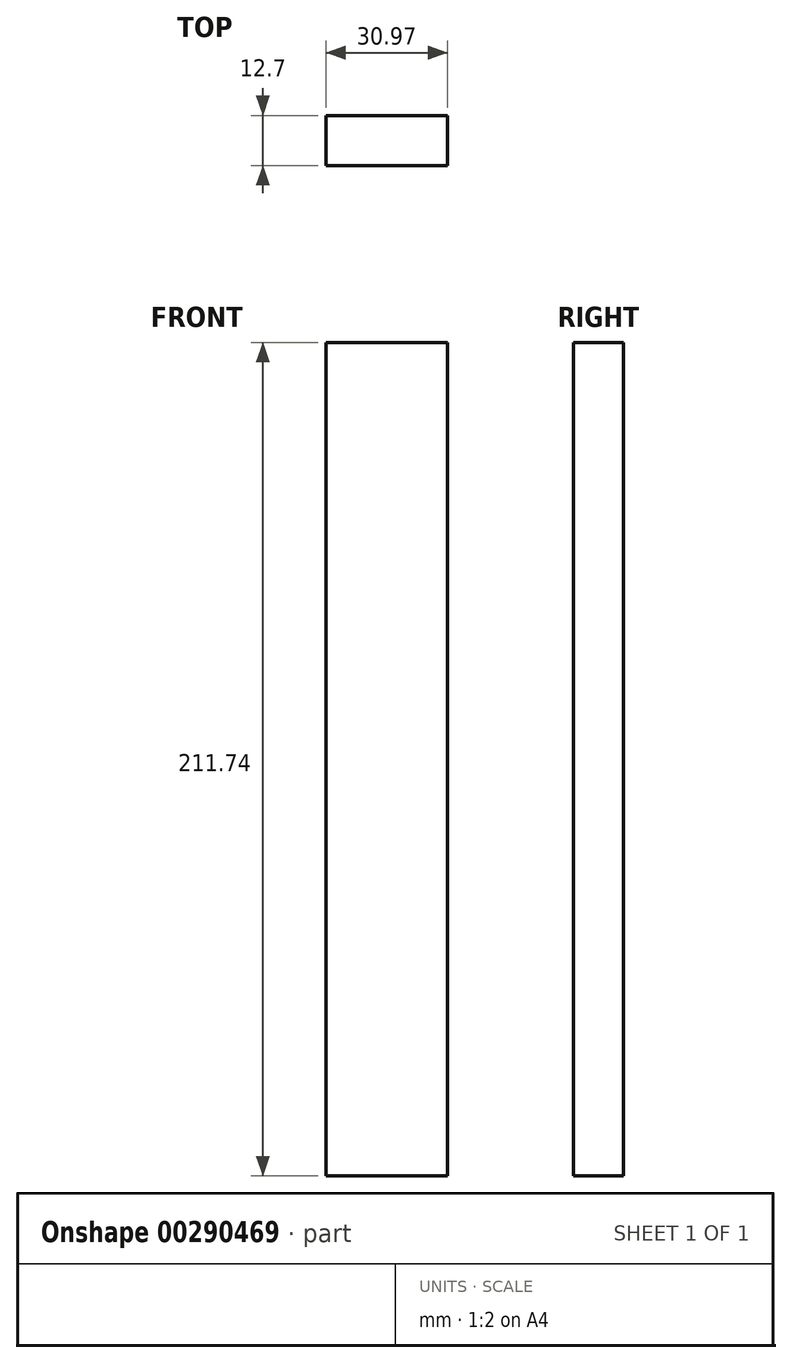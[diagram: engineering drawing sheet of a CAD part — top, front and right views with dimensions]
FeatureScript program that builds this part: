
annotation { "Feature Type Name" : "Feature", "Feature Type Description" : "" }
export const myFeature = defineFeature(function(context is Context, id is Id, definition is map)
    precondition{}
    {
        {
            var Q0;
            Q0=qCreatedBy(makeId("Front.planeOp"),FACE);
            var sketch = newSketch(context, id + "F0", { "sketchPlane" : qUnion([Q0])});
            skLineSegment(sketch, "E0.bottom", {"start": v(-50.7, 61.73) * mm, "end": v(-19.73, 61.73) * mm});
            skLineSegment(sketch, "E0.top", {"start": v(-50.7, -150.01) * mm, "end": v(-19.73, -150.01) * mm});
            skLineSegment(sketch, "E0.left", {"start": v(-50.7, 61.73) * mm, "end": v(-50.7, -150.01) * mm});
            skLineSegment(sketch, "E0.right", {"start": v(-19.73, 61.73) * mm, "end": v(-19.73, -150.01) * mm});
            skSolve(sketch);
        }
        {
            var Q0;
            Q0=makeQuery(id+"F0.imprint","IMPRINT",FACE,{"disambiguationData":[TD([[makeQuery(id+"F0.imprint","IMPRINT",EDGE,{"derivedFrom":sQuery(id+"F0.wireOp",EDGE,"E0.bottom")}),-1.0]])]});
            extrude(context, id + "F1", {"entities" : qUnion([Q0]), "depth" : 12.7 * mm});
        }
    });
